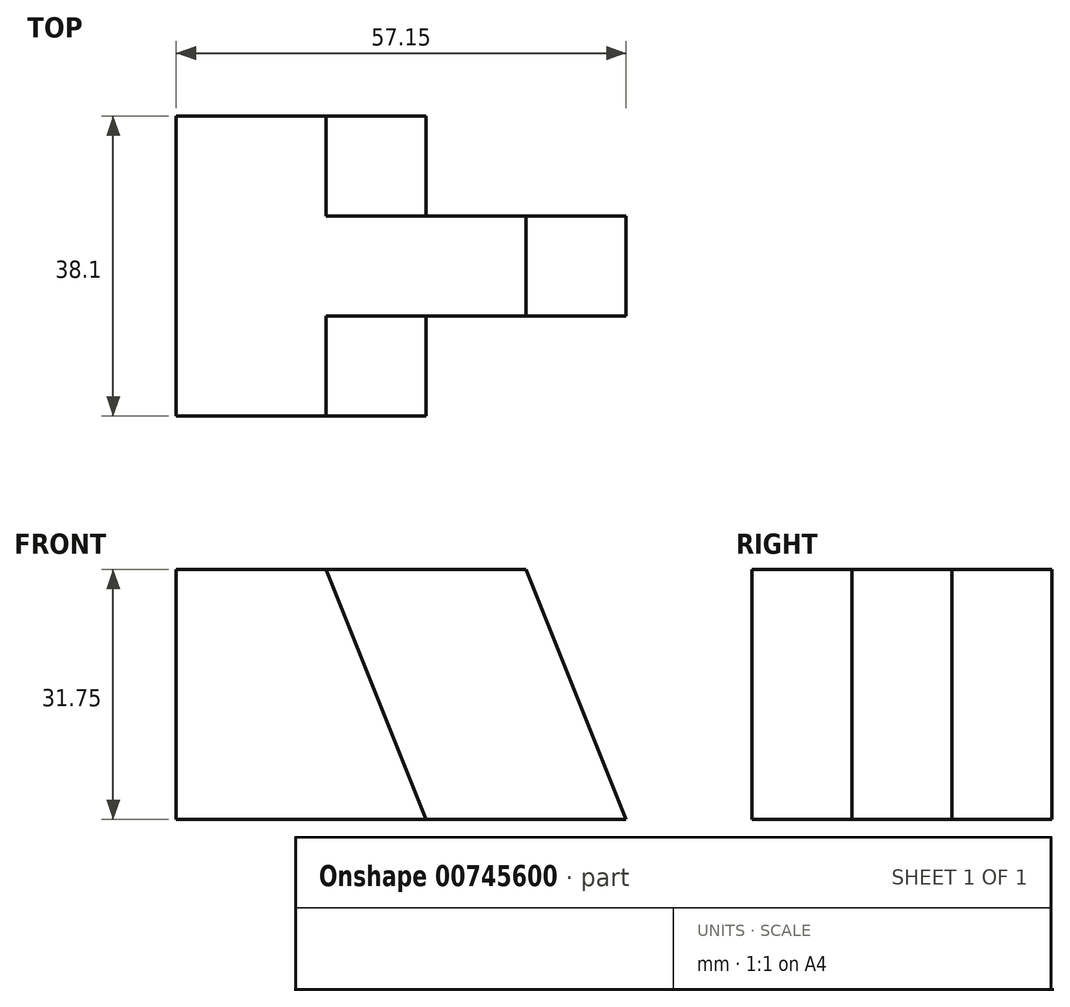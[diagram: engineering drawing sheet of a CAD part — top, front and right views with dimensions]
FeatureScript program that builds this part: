
annotation { "Feature Type Name" : "Feature", "Feature Type Description" : "" }
export const myFeature = defineFeature(function(context is Context, id is Id, definition is map)
    precondition{}
    {
        {
            var Q0;
            Q0=qCreatedBy(makeId("Top.planeOp"),FACE);
            var sketch = newSketch(context, id + "F0", { "sketchPlane" : qUnion([Q0])});
            skLineSegment(sketch, "E0", {"start": v(0, 0) * mm, "end": v(0, 38.1) * mm});
            skLineSegment(sketch, "E1", {"start": v(0, 38.1) * mm, "end": v(31.75, 38.1) * mm});
            skLineSegment(sketch, "E2", {"start": v(31.75, 38.1) * mm, "end": v(31.75, 25.4) * mm});
            skLineSegment(sketch, "E3", {"start": v(57.15, 25.4) * mm, "end": v(57.15, 12.7) * mm});
            skLineSegment(sketch, "E4", {"start": v(57.15, 12.7) * mm, "end": v(31.75, 12.7) * mm});
            skLineSegment(sketch, "E5", {"start": v(31.75, 12.7) * mm, "end": v(31.75, 0) * mm});
            skLineSegment(sketch, "E6", {"start": v(57.15, 25.4) * mm, "end": v(31.75, 25.4) * mm});
            skLineSegment(sketch, "E7", {"start": v(0, 0) * mm, "end": v(31.75, 0) * mm});
            skSolve(sketch);
        }
        {
            var Q0;
            Q0 = qSketchRegion(id + "F0", true);
            extrude(context, id + "F1", {"entities" : qUnion([Q0]), "depth" : 31.75 * mm, "offsetDistance" : 25.4 * mm});
        }
        {
            var Q0;
            Q0=makeQuery(id+"F1.opExtrude","SWEPT_FACE",FACE,{"disambiguationData":[OSD([sQuery(id+"F0.wireOp",EDGE,"E7")])]});
            var sketch = newSketch(context, id + "F2", { "sketchPlane" : qUnion([Q0])});
            skLineSegment(sketch, "E8", {"start": v(19.05, 31.75) * mm, "end": v(31.75, 0) * mm});
            skLineSegment(sketch, "E9", {"start": v(31.75, 0) * mm, "end": v(31.75, 31.75) * mm});
            skLineSegment(sketch, "E10", {"start": v(31.75, 31.75) * mm, "end": v(19.05, 31.75) * mm});
            skSolve(sketch);
        }
        {
            var Q0;
            Q0=makeQuery(id+"F2.imprint","IMPRINT",FACE,{"disambiguationData":[TD([[makeQuery(id+"F2.imprint","IMPRINT",EDGE,{"derivedFrom":sQuery(id+"F2.wireOp",EDGE,"E8")}),1.0]])]});
            extrude(context, id + "F3", {"entities" : qUnion([Q0]), "operationType" : NewBodyOperationType.REMOVE, "oppositeDirection" : true, "depth" : 12.7 * mm, "offsetDistance" : 25.4 * mm});
        }
        {
            var Q0;
            Q0=makeQuery(id+"F1.opExtrude","SWEPT_FACE",FACE,{"disambiguationData":[OSD([sQuery(id+"F0.wireOp",EDGE,"E1")])]});
            var sketch = newSketch(context, id + "F4", { "sketchPlane" : qUnion([Q0])});
            skLineSegment(sketch, "E11", {"start": v(-19.05, 31.75) * mm, "end": v(-31.75, 0) * mm});
            skLineSegment(sketch, "E12", {"start": v(-31.75, 31.75) * mm, "end": v(-31.75, 0) * mm});
            skLineSegment(sketch, "E13", {"start": v(-19.05, 31.75) * mm, "end": v(-31.75, 31.75) * mm});
            skSolve(sketch);
        }
        {
            var Q0;
            Q0 = qSketchRegion(id + "F4", true);
            extrude(context, id + "F5", {"entities" : qUnion([Q0]), "operationType" : NewBodyOperationType.REMOVE, "oppositeDirection" : true, "depth" : 12.7 * mm, "offsetDistance" : 25.4 * mm});
        }
        {
            var Q0;
            Q0=makeQuery(id+"F5.boolean.opBoolean","MERGE",FACE,{"derivedFrom":[makeQuery(id+"F1.opExtrude","SWEPT_FACE",FACE,{"disambiguationData":[OSD([sQuery(id+"F0.wireOp",EDGE,"E6")])]}),makeQuery(id+"F5.opExtrude","CAP_FACE",FACE,{"disambiguationData":[OSD([sQuery(id+"F4.wireOp",EDGE,"E11"),sQuery(id+"F4.wireOp",EDGE,"E12"),sQuery(id+"F4.wireOp",EDGE,"E13")])],"isStart":false})]});
            var sketch = newSketch(context, id + "F6", { "sketchPlane" : qUnion([Q0])});
            skLineSegment(sketch, "E14", {"start": v(-44.45, 31.75) * mm, "end": v(-57.15, 0) * mm});
            skLineSegment(sketch, "E15", {"start": v(-57.15, 0) * mm, "end": v(-57.15, 31.75) * mm});
            skLineSegment(sketch, "E16", {"start": v(-57.15, 31.75) * mm, "end": v(-44.45, 31.75) * mm});
            skSolve(sketch);
        }
        {
            var Q0;
            Q0 = qSketchRegion(id + "F6", true);
            extrude(context, id + "F7", {"entities" : qUnion([Q0]), "operationType" : NewBodyOperationType.REMOVE, "oppositeDirection" : true, "depth" : 12.7 * mm, "offsetDistance" : 25.4 * mm});
        }
    });
